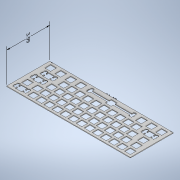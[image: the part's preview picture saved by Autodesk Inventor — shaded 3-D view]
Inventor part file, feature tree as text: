
AUTODESK INVENTOR PART (.ipt)
format: ipt  version: 2022 (Build 260153000, 153)  size: 584,704 bytes
history: native  units: in
note: dims shown in document units (in); Inventor stores cm internally (conversion verified against a paired STEP export)
features: other x3, extrude x1, sketch x1
ambient origin geometry x8: Origin, YZ Plane, XZ Plane, XY Plane, X Axis, Y Axis, Z Axis, Center Point
bodies: Solid1 (feature_tree)
feature tree (5):
  other  "Annotations"
  extrude  "Extrusion1"  Depth=11.4862in TaperAngle=0.0deg
  sketch  "Sketch1"  dims[d0=0.0591in d1=0.0in d2=11.4862in d3=0.0in d4=0.3937in d5=3.9862in]
  other  "Linear Dimension 1"
  other  "Linear Dimension 2"
